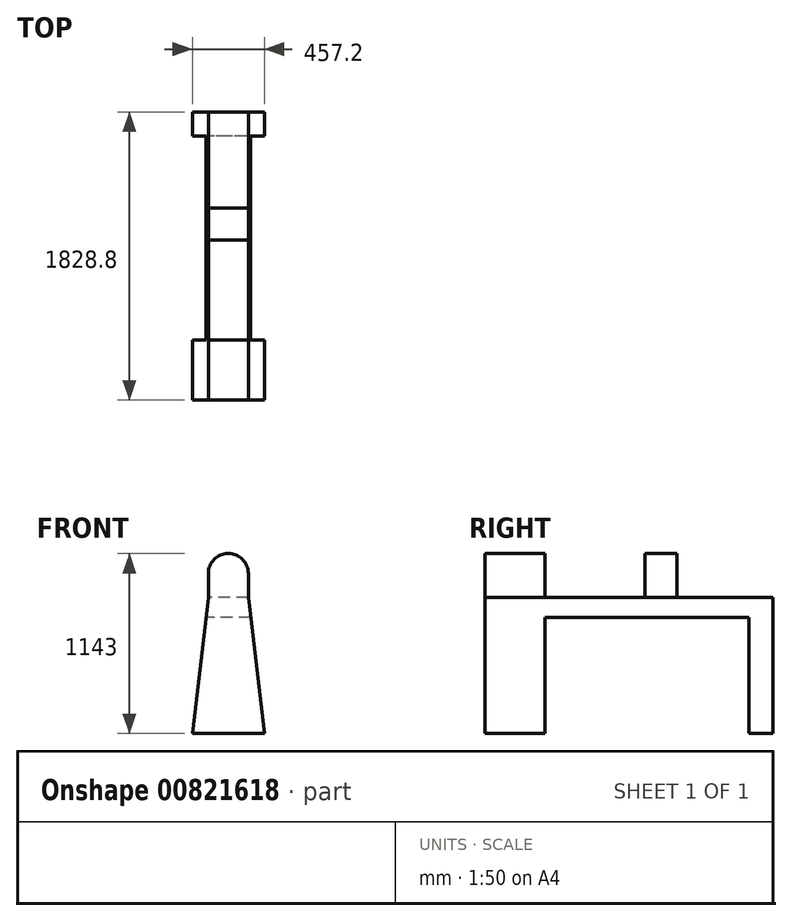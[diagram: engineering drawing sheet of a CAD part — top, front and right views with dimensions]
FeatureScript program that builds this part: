
annotation { "Feature Type Name" : "Feature", "Feature Type Description" : "" }
export const myFeature = defineFeature(function(context is Context, id is Id, definition is map)
    precondition{}
    {
        {
            var Q0;
            Q0=qCreatedBy(makeId("Front.planeOp"),FACE);
            var sketch = newSketch(context, id + "F0", { "sketchPlane" : qUnion([Q0]), "disableImprinting" : false});
            skLineSegment(sketch, "E0", {"start": v(0, 0) * mm, "end": v(101.6, 863.6) * mm});
            skArc(sketch, "E1", {"start": v(355.6, 1016) * mm, "mid": v(228.6, 1143) * mm, "end": v(101.6, 1016) * mm});
            skLineSegment(sketch, "E2", {"start": v(355.6, 1016) * mm, "end": v(355.6, 863.6) * mm});
            skLineSegment(sketch, "E3", {"start": v(457.2, 0) * mm, "end": v(0, 0) * mm});
            skLineSegment(sketch, "E4.trimOffspring", {"start": v(355.6, 863.6) * mm, "end": v(457.2, 0) * mm});
            skLineSegment(sketch, "E5.trimOffspring", {"start": v(101.6, 863.6) * mm, "end": v(101.6, 1016) * mm});
            skLineSegment(sketch, "E6", {"start": v(228.6, 1016) * mm, "end": v(228.6, 0) * mm, "construction": true});
            skSolve(sketch);
        }
        {
            var Q0;
            Q0 = qSketchRegion(id + "F0", true);
            extrude(context, id + "F1", {"entities" : qUnion([Q0]), "depth" : 1828.8 * mm, "offsetDistance" : 25.4 * mm});
        }
        {
            var Q0;
            Q0=qCreatedBy(makeId("Right.planeOp"),FACE);
            var sketch = newSketch(context, id + "F2", { "sketchPlane" : qUnion([Q0]), "disableImprinting" : false});
            skLineSegment(sketch, "E7.bottom", {"start": v(-1447.8, 0) * mm, "end": v(-152.4, 0) * mm});
            skLineSegment(sketch, "E7.top", {"start": v(-1447.8, 736.6) * mm, "end": v(-152.4, 736.6) * mm});
            skLineSegment(sketch, "E7.left", {"start": v(-1447.8, 0) * mm, "end": v(-1447.8, 736.6) * mm});
            skLineSegment(sketch, "E7.right", {"start": v(-152.4, 0) * mm, "end": v(-152.4, 736.6) * mm});
            skLineSegment(sketch, "E8.bottom", {"start": v(-812.8, 863.6) * mm, "end": v(-1447.8, 863.6) * mm});
            skLineSegment(sketch, "E8.top", {"start": v(-812.8, 1143) * mm, "end": v(-1447.8, 1143) * mm});
            skLineSegment(sketch, "E8.left", {"start": v(-812.8, 863.6) * mm, "end": v(-812.8, 1143) * mm});
            skLineSegment(sketch, "E8.right", {"start": v(-1447.8, 863.6) * mm, "end": v(-1447.8, 1143) * mm});
            skLineSegment(sketch, "E9.bottom", {"start": v(-609.6, 1143) * mm, "end": v(0, 1143) * mm});
            skLineSegment(sketch, "E9.top", {"start": v(-609.6, 863.6) * mm, "end": v(0, 863.6) * mm});
            skLineSegment(sketch, "E9.left", {"start": v(-609.6, 1143) * mm, "end": v(-609.6, 863.6) * mm});
            skLineSegment(sketch, "E9.right", {"start": v(0, 1143) * mm, "end": v(0, 863.6) * mm});
            skSolve(sketch);
        }
        {
            var Q0;
            Q0 = qSketchRegion(id + "F2", true);
            extrude(context, id + "F3", {"entities" : qUnion([Q0]), "operationType" : NewBodyOperationType.REMOVE, "endBound" : BoundingType.THROUGH_ALL, "depth" : 25.4 * mm, "offsetDistance" : 25.4 * mm});
        }
    });
